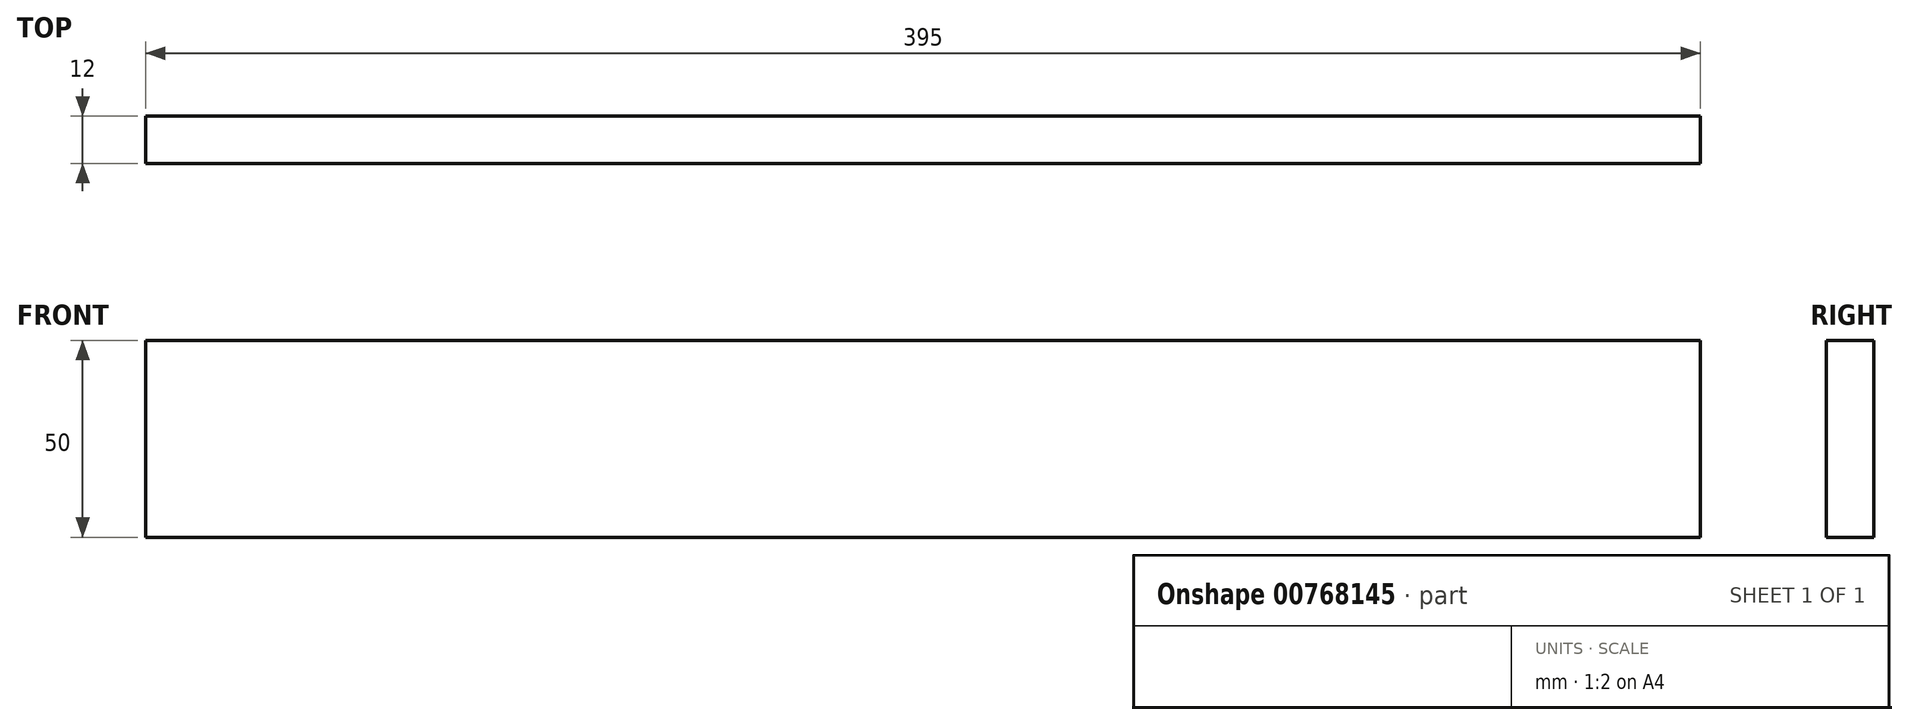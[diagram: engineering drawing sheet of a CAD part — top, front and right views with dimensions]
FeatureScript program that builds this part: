
annotation { "Feature Type Name" : "Feature", "Feature Type Description" : "" }
export const myFeature = defineFeature(function(context is Context, id is Id, definition is map)
    precondition{}
    {
        {
            var Q0;
            Q0=qCreatedBy(makeId("Front.planeOp"),FACE);
            var sketch = newSketch(context, id + "F0", { "sketchPlane" : qUnion([Q0])});
            skLineSegment(sketch, "E0.bottom", {"start": v(197.5, 25) * mm, "end": v(-197.5, 25) * mm});
            skLineSegment(sketch, "E0.top", {"start": v(197.5, -25) * mm, "end": v(-197.5, -25) * mm});
            skLineSegment(sketch, "E0.left", {"start": v(197.5, 25) * mm, "end": v(197.5, -25) * mm});
            skLineSegment(sketch, "E0.right", {"start": v(-197.5, 25) * mm, "end": v(-197.5, -25) * mm});
            skPoint(sketch, "E0.middle", {"position": v(0, 0) * mm});
            skSolve(sketch);
        }
        {
            var Q0;
            Q0 = qSketchRegion(id + "F0", true);
            extrude(context, id + "F1", {"entities" : qUnion([Q0]), "depth" : 12 * mm, "offsetDistance" : 25 * mm});
        }
    });
